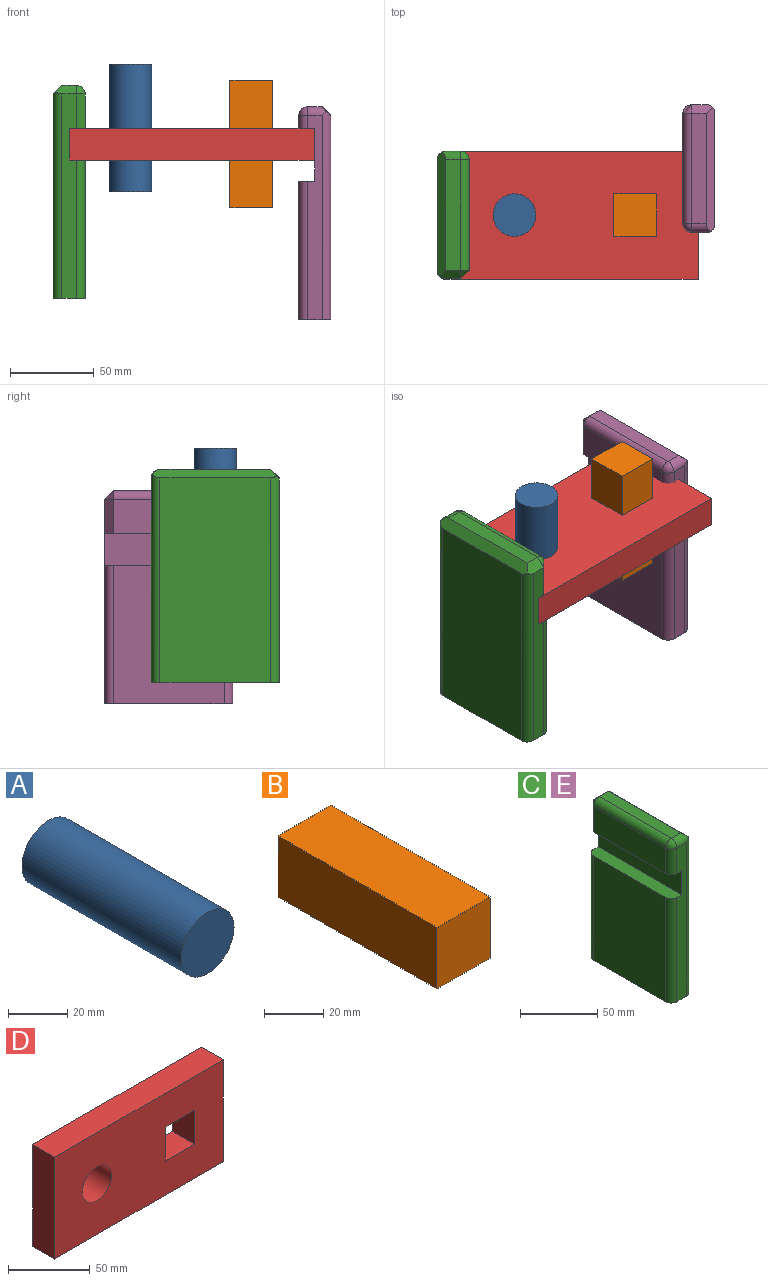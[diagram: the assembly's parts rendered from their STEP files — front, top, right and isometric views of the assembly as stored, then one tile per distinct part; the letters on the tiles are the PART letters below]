
ASSEMBLY  parts=5 mates=3
PART A: 3 faces, bbox 25.4x76.2x25.4 mm
  f0: cylinder r=12.7mm len=76.2mm, axis (0,1,0), area 6080.5mm2, adj f1,f2
  f1: plane 25.4x25.4mm, normal (0,-1,0), area 506.7mm2, adj f0
  f2: plane 25.4x25.4mm, normal (0,1,0), area 506.7mm2, adj f0
PART B: 6 faces, bbox 25.4x76.2x25.4 mm
  f0: plane 76.2x25.4mm, normal (1,0,0), area 1935.5mm2, adj f1,f3,f4,f5
  f1: plane 76.2x25.4mm, normal (0,0,1), area 1935.5mm2, adj f0,f2,f4,f5
  f2: plane 76.2x25.4mm, normal (-1,0,0), area 1935.5mm2, adj f1,f3,f4,f5
  f3: plane 76.2x25.4mm, normal (0,0,-1), area 1935.5mm2, adj f0,f2,f4,f5
  f4: plane 25.4x25.4mm, normal (0,-1,0), area 645.2mm2, adj f0,f1,f2,f3
  f5: plane 25.4x25.4mm, normal (0,1,0), area 645.2mm2, adj f0,f1,f2,f3
PART C: 22 faces, bbox 19.1x76.2x127 mm
  f0: plane 82.55x66.04mm, normal (-1,0,0), area 5451.6mm2, adj f1,f7,f19,f21
  f1: plane 76.2x19.05mm, normal (0,0,-1), area 1429.5mm2, adj f0,f2,f8,f9,f18,f19,f20,f21
  f2: plane 121.92x66.04mm, normal (1,0,0), area 8051.6mm2, adj f1,f10,f18,f20
  f3: plane 66.04x8.89mm, normal (0,0,1), area 587.1mm2, adj f10,f11,f12,f15
  f4: plane 66.04x20.32mm, normal (-1,0,0), area 1341.9mm2, adj f5,f11,f14,f17
  f5: plane 76.2x9.53mm, normal (0,0,-1), area 707.4mm2, adj f4,f6,f8,f9,f14,f17
  f6: plane 76.2x19.05mm, normal (-1,0,0), area 1451.6mm2, adj f5,f7,f8,f9
  f7: plane 76.2x9.53mm, normal (0,0,1), area 714.7mm2, adj f0,f6,f8,f9,f19,f21
  f8: plane 121.92x8.89mm, normal (0,-1,0), area 999.2mm2, adj f1,f5,f6,f7,f12,f14,f20,f21
  f9: plane 121.92x8.89mm, normal (0,1,0), area 999.2mm2, adj f1,f5,f6,f7,f15,f17,f18,f19
  f10: plane 74.03x5.08mm, normal (0.71,0,0.71), area 511.2mm2, adj f2,f3,f12,f15,f18,f20
  f11: cylinder r=5.08mm len=66.04mm, axis (0,1,0), area 527mm2, adj f3,f4,f13,f16
  f12: cylinder r=5.08mm len=11.43mm, axis (1,0,0), area 79.1mm2, adj f3,f8,f10,f13,f20
  f13: sphere r=5.08mm, area 40.5mm2, adj f11,f12,f14
  f14: cylinder r=5.08mm len=20.32mm, axis (0,0,1), area 162.1mm2, adj f4,f5,f8,f13
  f15: plane 12.48x5.08mm, normal (0,0.71,0.71), area 78.2mm2, adj f3,f9,f10,f16,f18
  f16: cone r=5.08mm half-angle=45deg, axis (0,-1,0), area 28.7mm2, adj f11,f15,f17
  f17: plane 20.32x5.08mm, normal (-0.71,0.71,0), area 146mm2, adj f4,f5,f9,f16
  f18: cylinder r=5.08mm len=123.41mm, axis (0,0,1), area 976.9mm2, adj f1,f2,f9,f10,f15
  f19: cylinder r=5.08mm len=82.55mm, axis (0,0,-1), area 658.7mm2, adj f0,f1,f7,f9
  f20: cylinder r=5.08mm len=124.46mm, axis (0,0,-1), area 981mm2, adj f1,f2,f8,f10,f12
  f21: cylinder r=5.08mm len=82.55mm, axis (0,0,1), area 658.7mm2, adj f0,f1,f7,f8
PART D: 11 faces, bbox 146.1x19.1x76.2 mm
  f0: plane 76.2x19.05mm, normal (1,0,0), area 1451.6mm2, adj f1,f8,f9,f10
  f1: plane 146.05x19.05mm, normal (0,0,1), area 2782.3mm2, adj f0,f2,f9,f10
  f2: plane 76.2x19.05mm, normal (-1,0,0), area 1451.6mm2, adj f1,f8,f9,f10
  f3: plane 25.4x19.05mm, normal (0,0,1), area 483.9mm2, adj f4,f6,f9,f10
  f4: plane 25.4x19.05mm, normal (1,0,0), area 483.9mm2, adj f3,f5,f9,f10
  f5: plane 25.4x19.05mm, normal (0,0,-1), area 483.9mm2, adj f4,f6,f9,f10
  f6: plane 25.4x19.05mm, normal (-1,0,0), area 483.9mm2, adj f3,f5,f9,f10
  f7: cylinder r=12.7mm len=25.4mm, axis (0,1,0), area 1520.1mm2, adj f9,f10
  f8: plane 146.05x19.05mm, normal (0,0,-1), area 2782.3mm2, adj f0,f2,f9,f10
  f9: plane 146.05x76.2mm, normal (0,-1,0), area 9977.1mm2, adj f0,f1,f2,f3,f4,f5,f6,f7
  f10: plane 146.05x76.2mm, normal (0,1,0), area 9977.1mm2, adj f0,f1,f2,f3,f4,f5,f6,f7
PART E: same geometry as C
PLACE A rot(axis=(1,0,0),90deg) t=(-129.39,-20.06,111.6)mm fixed
PLACE B rot(axis=(1,0,0),90deg) t=(-49,-13.7,102.07)mm
PLACE C rot(axis=(0,0,1),180deg) t=(-179.81,-64.5,-28.1)mm fixed
PLACE D rot(axis=(1,0,0),90deg) t=(-24.23,11.7,73.5)mm fixed
PLACE E t=(-14.22,39.49,-40.84)mm
MATE planar B.f3 <-> D.f3  axis (0,1,0) through (-61.7,-13.7,63.97)mm
MATE planar C.f6 <-> D.f2  axis (1,0,0) through (-170.28,-26.4,63.97)mm
MATE slider A.f0 <-> D.f7  axis (0,0,1) through (-133.77,-26.4,73.5)mm
